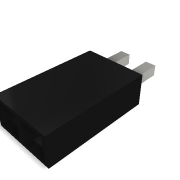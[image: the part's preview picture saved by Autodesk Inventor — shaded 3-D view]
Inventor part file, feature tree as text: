
AUTODESK INVENTOR PART (.ipt)
format: ipt  version: 2020 (Build 240168000, 168)  size: 192,512 bytes
history: native  units: in
note: dims shown in document units (in); Inventor stores cm internally (conversion verified against a paired STEP export)
features: extrude x3, sketch x3, chamfer x2, other x2, pattern_linear x1
ambient origin geometry x8: Origin, YZ Plane, XZ Plane, XY Plane, X Axis, Y Axis, Z Axis, Center Point
bodies: Solid1 (feature_tree)
feature tree (11):
  extrude  "Extrusion1"  Depth=0.1in
  extrude  "Extrusion2"  Depth=0.045in
  chamfer  "Chamfer1"  Distance=0.25in
  extrude  "Extrusion3"  Depth=0.035in
  chamfer  "Chamfer2"  Distance=0.13in
  pattern_linear  "Rectangular Pattern1"  Spacing1=0.015in  [1 undecoded]
  other  "Work Axis1"
  sketch  "Sketch1"  dims[d0=0.1in d1=0.1in]
  sketch  "Sketch2"  dims[d2=0.33in d3=0.0in d4=0.045in d5=0.25in d6=0.0in]
  sketch  "Sketch3"  dims[d7=0.015in d8=0.125in d9=45.0deg d10=0.035in d11=0.13in d12=0.0in d13=0.015in d14=0.125in d15=45.0deg d16=0.7874in d18=0.1in]
  other  "Work Point1"
note: 1 required parameter value undecoded (feature->parameter linkage not recoverable at this tier; creation-order binding heuristic only, values carry confidence <= 0.55)
